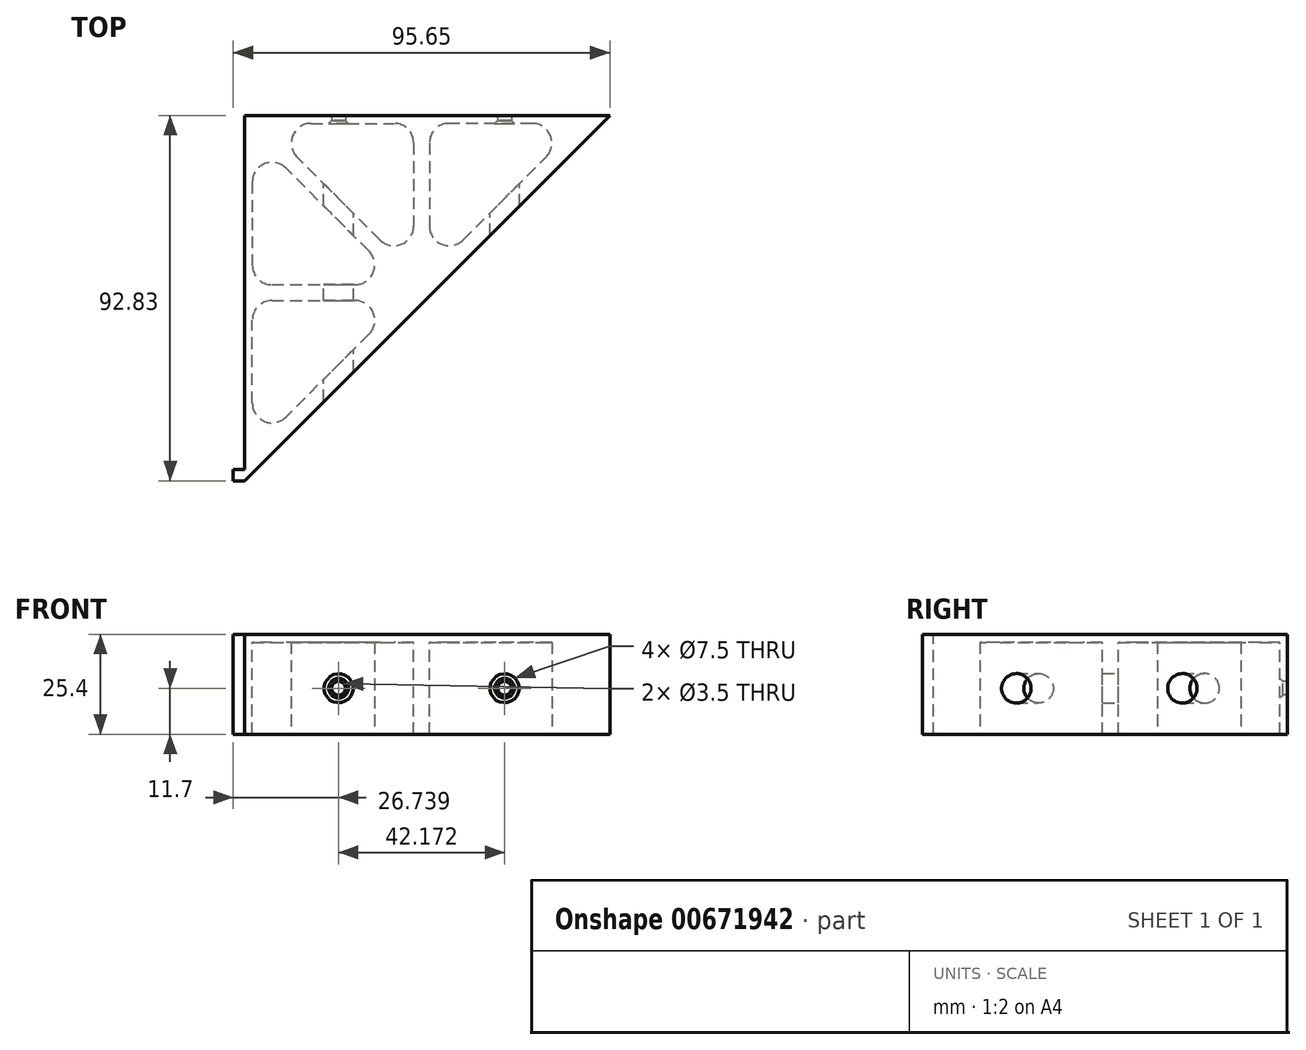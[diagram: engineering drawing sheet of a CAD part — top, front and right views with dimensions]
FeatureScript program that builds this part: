
annotation { "Feature Type Name" : "Feature", "Feature Type Description" : "" }
export const myFeature = defineFeature(function(context is Context, id is Id, definition is map)
    precondition{}
    {
        {
            var Q0;
            Q0=qCreatedBy(makeId("Top.planeOp"),FACE);
            var sketch = newSketch(context, id + "F0", { "sketchPlane" : qUnion([Q0])});
            skLineSegment(sketch, "E0", {"start": v(-35.18, -45) * mm, "end": v(-35.18, 45) * mm});
            skLineSegment(sketch, "E1", {"start": v(-35.18, 45) * mm, "end": v(54.82, 45) * mm});
            skLineSegment(sketch, "E2", {"start": v(-35.18, -45) * mm, "end": v(54.82, 45) * mm, "construction": true});
            skLineSegment(sketch, "E3", {"start": v(-35.18, 45) * mm, "end": v(9.82, 0) * mm, "construction": true});
            skLineSegment(sketch, "E4", {"start": v(9.82, 0) * mm, "end": v(9.82, 45) * mm, "construction": true});
            skLineSegment(sketch, "E5", {"start": v(9.82, 0) * mm, "end": v(-35.18, 0) * mm, "construction": true});
            skLineSegment(sketch, "E6", {"start": v(-33.18, -2) * mm, "end": v(5, -2) * mm});
            skLineSegment(sketch, "E7", {"start": v(5, -2) * mm, "end": v(-33.18, -40.17) * mm});
            skLineSegment(sketch, "E8", {"start": v(-33.18, -40.17) * mm, "end": v(-33.18, -2) * mm});
            skLineSegment(sketch, "E9.MirrorCS", {"start": v(5, 2) * mm, "end": v(-33.18, 40.17) * mm});
            skLineSegment(sketch, "E10.MirrorCS", {"start": v(-33.18, 2) * mm, "end": v(5, 2) * mm});
            skLineSegment(sketch, "E11.MirrorCS", {"start": v(-33.18, 40.17) * mm, "end": v(-33.18, 2) * mm});
            skLineSegment(sketch, "E12.MirrorCS", {"start": v(-30.35, 43) * mm, "end": v(7.82, 43) * mm});
            skLineSegment(sketch, "E13.MirrorCS", {"start": v(7.82, 4.83) * mm, "end": v(-30.35, 43) * mm});
            skLineSegment(sketch, "E14.MirrorCS", {"start": v(7.82, 43) * mm, "end": v(7.82, 4.83) * mm});
            skLineSegment(sketch, "E15.MirrorCS", {"start": v(50, 43) * mm, "end": v(11.82, 43) * mm});
            skLineSegment(sketch, "E16.MirrorCS", {"start": v(11.82, 43) * mm, "end": v(11.82, 4.83) * mm});
            skLineSegment(sketch, "E17.MirrorCS", {"start": v(11.82, 4.83) * mm, "end": v(50, 43) * mm});
            skLineSegment(sketch, "E18", {"start": v(-35.18, -45) * mm, "end": v(-35.18, -47.83) * mm});
            skLineSegment(sketch, "E19", {"start": v(-35.18, -47.83) * mm, "end": v(57.65, 45) * mm});
            skLineSegment(sketch, "E20", {"start": v(57.65, 45) * mm, "end": v(54.82, 45) * mm});
            skLineSegment(sketch, "E21", {"start": v(-35.18, -47.83) * mm, "end": v(-38, -47.83) * mm});
            skLineSegment(sketch, "E22", {"start": v(-38, -47.83) * mm, "end": v(-38, -45) * mm});
            skLineSegment(sketch, "E23", {"start": v(-38, -45) * mm, "end": v(-35.18, -45) * mm});
            skSolve(sketch);
        }
        {
            var Q0;
            {var subQ0=sQuery(id+"F0.wireOp",EDGE,"E2");var subQ1=sQuery(id+"F0.wireOp",EDGE,"E0");var subQ2=makeQuery(id+"F0.imprint","INTERSECT",VERTEX,{"derivedFrom":[subQ1,subQ0]});Q0=makeQuery(id+"F0.imprint","IMPRINT",FACE,{"disambiguationData":[TD([[makeQuery(id+"F0.imprint","IMPRINT",EDGE,{"disambiguationData":[TD([[subQ2,-1.0]])],"derivedFrom":subQ1}),-1.0]])]});}
            var Q1;
            {var subQ3=sQuery(id+"F0.wireOp",EDGE,"E5");var subQ5=sQuery(id+"F0.wireOp",EDGE,"E2");var subQ6=makeQuery(id+"F0.imprint","INTERSECT",VERTEX,{"derivedFrom":[subQ5,subQ3]});Q1=makeQuery(id+"F0.imprint","IMPRINT",FACE,{"disambiguationData":[TD([[makeQuery(id+"F0.imprint","IMPRINT",EDGE,{"disambiguationData":[TD([[subQ6,-1.0]])],"derivedFrom":subQ5}),1.0]])]});}
            var Q2;
            {var subQ3=sQuery(id+"F0.wireOp",EDGE,"E4");var subQ5=sQuery(id+"F0.wireOp",EDGE,"E2");var subQ6=makeQuery(id+"F0.imprint","INTERSECT",VERTEX,{"derivedFrom":[subQ5,subQ3]});Q2=makeQuery(id+"F0.imprint","IMPRINT",FACE,{"disambiguationData":[TD([[makeQuery(id+"F0.imprint","IMPRINT",EDGE,{"disambiguationData":[TD([[subQ6,1.0]])],"derivedFrom":subQ5}),1.0]])]});}
            var Q3;
            {var subQ0=sQuery(id+"F0.wireOp",EDGE,"E2");var subQ1=sQuery(id+"F0.wireOp",EDGE,"E1");var subQ2=makeQuery(id+"F0.imprint","INTERSECT",VERTEX,{"derivedFrom":[subQ1,subQ0]});Q3=makeQuery(id+"F0.imprint","IMPRINT",FACE,{"disambiguationData":[TD([[makeQuery(id+"F0.imprint","IMPRINT",EDGE,{"disambiguationData":[TD([[subQ2,1.0]])],"derivedFrom":subQ1}),-1.0]])]});}
            var Q4;
            Q4=makeQuery(id+"F0.imprint","IMPRINT",FACE,{"disambiguationData":[TD([[makeQuery(id+"F0.imprint","IMPRINT",EDGE,{"derivedFrom":sQuery(id+"F0.wireOp",EDGE,"E18")}),-1.0]])]});
            extrude(context, id + "F1", {"entities" : qUnion([Q0, Q1, Q2, Q3, Q4]), "oppositeDirection" : true, "depth" : 25.4 * mm, "offsetDistance" : 25 * mm});
        }
        {
            var Q0;
            Q0=makeQuery(id+"F0.imprint","IMPRINT",FACE,{"disambiguationData":[TD([[makeQuery(id+"F0.imprint","IMPRINT",EDGE,{"derivedFrom":sQuery(id+"F0.wireOp",EDGE,"E9.MirrorCS")}),1.0]])]});
            var Q1;
            Q1=makeQuery(id+"F0.imprint","IMPRINT",FACE,{"disambiguationData":[TD([[makeQuery(id+"F0.imprint","IMPRINT",EDGE,{"derivedFrom":sQuery(id+"F0.wireOp",EDGE,"E6")}),-1.0]])]});
            var Q2;
            Q2=makeQuery(id+"F0.imprint","IMPRINT",FACE,{"disambiguationData":[TD([[makeQuery(id+"F0.imprint","IMPRINT",EDGE,{"derivedFrom":sQuery(id+"F0.wireOp",EDGE,"E12.MirrorCS")}),-1.0]])]});
            var Q3;
            Q3=makeQuery(id+"F0.imprint","IMPRINT",FACE,{"disambiguationData":[TD([[makeQuery(id+"F0.imprint","IMPRINT",EDGE,{"derivedFrom":sQuery(id+"F0.wireOp",EDGE,"E15.MirrorCS")}),1.0]])]});
            extrude(context, id + "F2", {"entities" : qUnion([Q0, Q1, Q2, Q3]), "operationType" : NewBodyOperationType.ADD, "oppositeDirection" : true, "depth" : 2 * mm, "offsetDistance" : 25 * mm});
        }
        {
            var Q0;
            Q0=makeQuery(id+"F1.opExtrude","SWEPT_FACE",FACE,{"disambiguationData":[OSD([sQuery(id+"F0.wireOp",EDGE,"E12.MirrorCS")])]});
            var sketch = newSketch(context, id + "F3", { "sketchPlane" : qUnion([Q0])});
            skLineSegment(sketch, "E24", {"start": v(-30.35, -13.7) * mm, "end": v(7.82, -13.7) * mm, "construction": true});
            skLineSegment(sketch, "E25", {"start": v(-11.26, -13.7) * mm, "end": v(-11.26, -2) * mm, "construction": true});
            skCircle(sketch, "E26", {"center": v(-11.26, -13.7) * mm, "radius": 3.75 * mm});
            skCircle(sketch, "E27", {"center": v(-11.26, -13.7) * mm, "radius": 2.25 * mm});
            skSolve(sketch);
        }
        {
            var Q0;
            Q0=makeQuery(id+"F1.opExtrude","SWEPT_FACE",FACE,{"disambiguationData":[OSD([sQuery(id+"F0.wireOp",EDGE,"E15.MirrorCS")])]});
            var sketch = newSketch(context, id + "F4", { "sketchPlane" : qUnion([Q0])});
            skLineSegment(sketch, "E28", {"start": v(11.82, -13.7) * mm, "end": v(50, -13.7) * mm, "construction": true});
            skLineSegment(sketch, "E29", {"start": v(30.91, -2) * mm, "end": v(30.91, -13.7) * mm, "construction": true});
            skSolve(sketch);
        }
        {
            var Q0;
            Q0=sQuery(id+"F3.wireOp",VERTEX,"E27.center");
            var Q1;
            Q1=sQuery(id+"F4.wireOp",VERTEX,"E29.end");
            var Q2;
            Q2=makeQuery(id+"F1.opExtrude","SWEPT_BODY",BODY,{"disambiguationData":[OSD([sQuery(id+"F0.wireOp",EDGE,"E0"),sQuery(id+"F0.wireOp",EDGE,"E1"),sQuery(id+"F0.wireOp",EDGE,"E6"),sQuery(id+"F0.wireOp",EDGE,"E7"),sQuery(id+"F0.wireOp",EDGE,"E8"),sQuery(id+"F0.wireOp",EDGE,"E9.MirrorCS"),sQuery(id+"F0.wireOp",EDGE,"E10.MirrorCS"),sQuery(id+"F0.wireOp",EDGE,"E11.MirrorCS"),sQuery(id+"F0.wireOp",EDGE,"E12.MirrorCS"),sQuery(id+"F0.wireOp",EDGE,"E13.MirrorCS"),sQuery(id+"F0.wireOp",EDGE,"E14.MirrorCS"),sQuery(id+"F0.wireOp",EDGE,"E15.MirrorCS"),sQuery(id+"F0.wireOp",EDGE,"E16.MirrorCS"),sQuery(id+"F0.wireOp",EDGE,"E17.MirrorCS"),sQuery(id+"F0.wireOp",EDGE,"E19"),sQuery(id+"F0.wireOp",EDGE,"E20"),sQuery(id+"F0.wireOp",EDGE,"E21"),sQuery(id+"F0.wireOp",EDGE,"E22"),sQuery(id+"F0.wireOp",EDGE,"E23")])]});
            hole(context, id + "F5", {"style" : HoleStyle.C_SINK, "endStyle" : HoleEndStyle.THROUGH, "holeDiameter" : 3.5 * mm, "cSinkDiameter" : 5 * mm, "cSinkAngle" : 90 * degree, "majorDiameter" : 5 * mm, "isTappedThrough" : true, "tappedDepth" : 12 * mm, "tapClearance" : 3, "locations" : qUnion([Q0, Q1]), "scope" : qUnion([Q2])});
        }
        {
            var Q0;
            Q0=sQuery(id+"F3.wireOp",VERTEX,"E27.center");
            var Q1;
            Q1=sQuery(id+"F4.wireOp",VERTEX,"E29.end");
            var Q2;
            Q2=makeQuery(id+"F1.opExtrude","SWEPT_BODY",BODY,{"disambiguationData":[OSD([sQuery(id+"F0.wireOp",EDGE,"E0"),sQuery(id+"F0.wireOp",EDGE,"E1"),sQuery(id+"F0.wireOp",EDGE,"E6"),sQuery(id+"F0.wireOp",EDGE,"E7"),sQuery(id+"F0.wireOp",EDGE,"E8"),sQuery(id+"F0.wireOp",EDGE,"E9.MirrorCS"),sQuery(id+"F0.wireOp",EDGE,"E10.MirrorCS"),sQuery(id+"F0.wireOp",EDGE,"E11.MirrorCS"),sQuery(id+"F0.wireOp",EDGE,"E12.MirrorCS"),sQuery(id+"F0.wireOp",EDGE,"E13.MirrorCS"),sQuery(id+"F0.wireOp",EDGE,"E14.MirrorCS"),sQuery(id+"F0.wireOp",EDGE,"E15.MirrorCS"),sQuery(id+"F0.wireOp",EDGE,"E16.MirrorCS"),sQuery(id+"F0.wireOp",EDGE,"E17.MirrorCS"),sQuery(id+"F0.wireOp",EDGE,"E19"),sQuery(id+"F0.wireOp",EDGE,"E20"),sQuery(id+"F0.wireOp",EDGE,"E21"),sQuery(id+"F0.wireOp",EDGE,"E22"),sQuery(id+"F0.wireOp",EDGE,"E23")])]});
            hole(context, id + "F6", {"style" : HoleStyle.C_SINK, "endStyle" : HoleEndStyle.THROUGH, "oppositeDirection" : true, "holeDiameter" : 7.5 * mm, "cSinkDiameter" : 7.5 * mm, "cSinkAngle" : 90 * degree, "majorDiameter" : 5 * mm, "isTappedThrough" : true, "tappedDepth" : 12 * mm, "tapClearance" : 3, "locations" : qUnion([Q0, Q1]), "scope" : qUnion([Q2])});
        }
        {
            var Q0;
            Q0=makeQuery(id+"F1.opExtrude","SWEPT_EDGE",EDGE,{"disambiguationData":[OSD([sQuery(id+"F0.wireOp",EDGE,"E10.MirrorCS"),sQuery(id+"F0.wireOp",EDGE,"E11.MirrorCS")])]});
            var Q1;
            Q1=makeQuery(id+"F1.opExtrude","SWEPT_EDGE",EDGE,{"disambiguationData":[OSD([sQuery(id+"F0.wireOp",EDGE,"E6"),sQuery(id+"F0.wireOp",EDGE,"E8")])]});
            var Q2;
            Q2=makeQuery(id+"F1.opExtrude","SWEPT_EDGE",EDGE,{"disambiguationData":[OSD([sQuery(id+"F0.wireOp",EDGE,"E7"),sQuery(id+"F0.wireOp",EDGE,"E8")])]});
            var Q3;
            Q3=makeQuery(id+"F1.opExtrude","SWEPT_EDGE",EDGE,{"disambiguationData":[OSD([sQuery(id+"F0.wireOp",EDGE,"E6"),sQuery(id+"F0.wireOp",EDGE,"E7")])]});
            var Q4;
            Q4=makeQuery(id+"F1.opExtrude","SWEPT_EDGE",EDGE,{"disambiguationData":[OSD([sQuery(id+"F0.wireOp",EDGE,"E9.MirrorCS"),sQuery(id+"F0.wireOp",EDGE,"E10.MirrorCS")])]});
            var Q5;
            Q5=makeQuery(id+"F1.opExtrude","SWEPT_EDGE",EDGE,{"disambiguationData":[OSD([sQuery(id+"F0.wireOp",EDGE,"E9.MirrorCS"),sQuery(id+"F0.wireOp",EDGE,"E11.MirrorCS")])]});
            var Q6;
            Q6=makeQuery(id+"F1.opExtrude","SWEPT_EDGE",EDGE,{"disambiguationData":[OSD([sQuery(id+"F0.wireOp",EDGE,"E13.MirrorCS"),sQuery(id+"F0.wireOp",EDGE,"E14.MirrorCS")])]});
            var Q7;
            Q7=makeQuery(id+"F1.opExtrude","SWEPT_EDGE",EDGE,{"disambiguationData":[OSD([sQuery(id+"F0.wireOp",EDGE,"E16.MirrorCS"),sQuery(id+"F0.wireOp",EDGE,"E17.MirrorCS")])]});
            var Q8;
            Q8=makeQuery(id+"F1.opExtrude","SWEPT_EDGE",EDGE,{"disambiguationData":[OSD([sQuery(id+"F0.wireOp",EDGE,"E15.MirrorCS"),sQuery(id+"F0.wireOp",EDGE,"E16.MirrorCS")])]});
            var Q9;
            Q9=makeQuery(id+"F1.opExtrude","SWEPT_EDGE",EDGE,{"disambiguationData":[OSD([sQuery(id+"F0.wireOp",EDGE,"E12.MirrorCS"),sQuery(id+"F0.wireOp",EDGE,"E13.MirrorCS")])]});
            var Q10;
            Q10=makeQuery(id+"F1.opExtrude","SWEPT_EDGE",EDGE,{"disambiguationData":[OSD([sQuery(id+"F0.wireOp",EDGE,"E12.MirrorCS"),sQuery(id+"F0.wireOp",EDGE,"E14.MirrorCS")])]});
            var Q11;
            Q11=makeQuery(id+"F1.opExtrude","SWEPT_EDGE",EDGE,{"disambiguationData":[OSD([sQuery(id+"F0.wireOp",EDGE,"E15.MirrorCS"),sQuery(id+"F0.wireOp",EDGE,"E17.MirrorCS")])]});
            var Q12;
            Q12=makeQuery(id+"F2.opExtrude","CAP_EDGE",EDGE,{"disambiguationData":[OSD([sQuery(id+"F0.wireOp",EDGE,"E13.MirrorCS")])],"isStart":false});
            var Q13;
            Q13=makeQuery(id+"F2.opExtrude","CAP_EDGE",EDGE,{"disambiguationData":[OSD([sQuery(id+"F0.wireOp",EDGE,"E12.MirrorCS")])],"isStart":false});
            var Q14;
            Q14=makeQuery(id+"F2.opExtrude","CAP_EDGE",EDGE,{"disambiguationData":[OSD([sQuery(id+"F0.wireOp",EDGE,"E14.MirrorCS")])],"isStart":false});
            var Q15;
            Q15=makeQuery(id+"F2.opExtrude","CAP_EDGE",EDGE,{"disambiguationData":[OSD([sQuery(id+"F0.wireOp",EDGE,"E16.MirrorCS")])],"isStart":false});
            var Q16;
            Q16=makeQuery(id+"F2.opExtrude","CAP_EDGE",EDGE,{"disambiguationData":[OSD([sQuery(id+"F0.wireOp",EDGE,"E15.MirrorCS")])],"isStart":false});
            var Q17;
            Q17=makeQuery(id+"F2.opExtrude","CAP_EDGE",EDGE,{"disambiguationData":[OSD([sQuery(id+"F0.wireOp",EDGE,"E17.MirrorCS")])],"isStart":false});
            var Q18;
            Q18=makeQuery(id+"F2.opExtrude","CAP_EDGE",EDGE,{"disambiguationData":[OSD([sQuery(id+"F0.wireOp",EDGE,"E10.MirrorCS")])],"isStart":false});
            var Q19;
            Q19=makeQuery(id+"F2.opExtrude","CAP_EDGE",EDGE,{"disambiguationData":[OSD([sQuery(id+"F0.wireOp",EDGE,"E7")])],"isStart":false});
            var Q20;
            Q20=makeQuery(id+"F2.opExtrude","CAP_EDGE",EDGE,{"disambiguationData":[OSD([sQuery(id+"F0.wireOp",EDGE,"E9.MirrorCS")])],"isStart":false});
            var Q21;
            Q21=makeQuery(id+"F2.opExtrude","CAP_EDGE",EDGE,{"disambiguationData":[OSD([sQuery(id+"F0.wireOp",EDGE,"E11.MirrorCS")])],"isStart":false});
            var Q22;
            Q22=makeQuery(id+"F2.opExtrude","CAP_EDGE",EDGE,{"disambiguationData":[OSD([sQuery(id+"F0.wireOp",EDGE,"E8")])],"isStart":false});
            var Q23;
            Q23=makeQuery(id+"F2.opExtrude","CAP_EDGE",EDGE,{"disambiguationData":[OSD([sQuery(id+"F0.wireOp",EDGE,"E6")])],"isStart":false});
            fillet(context, id + "F7", {"entities" : qUnion([Q0, Q1, Q2, Q3, Q4, Q5, Q6, Q7, Q8, Q9, Q10, Q11, Q12, Q13, Q14, Q15, Q16, Q17, Q18, Q19, Q20, Q21, Q22, Q23]), "radius" : 5 * mm, "tangentPropagation" : true, "allowEdgeOverflow" : false});
        }
    });
